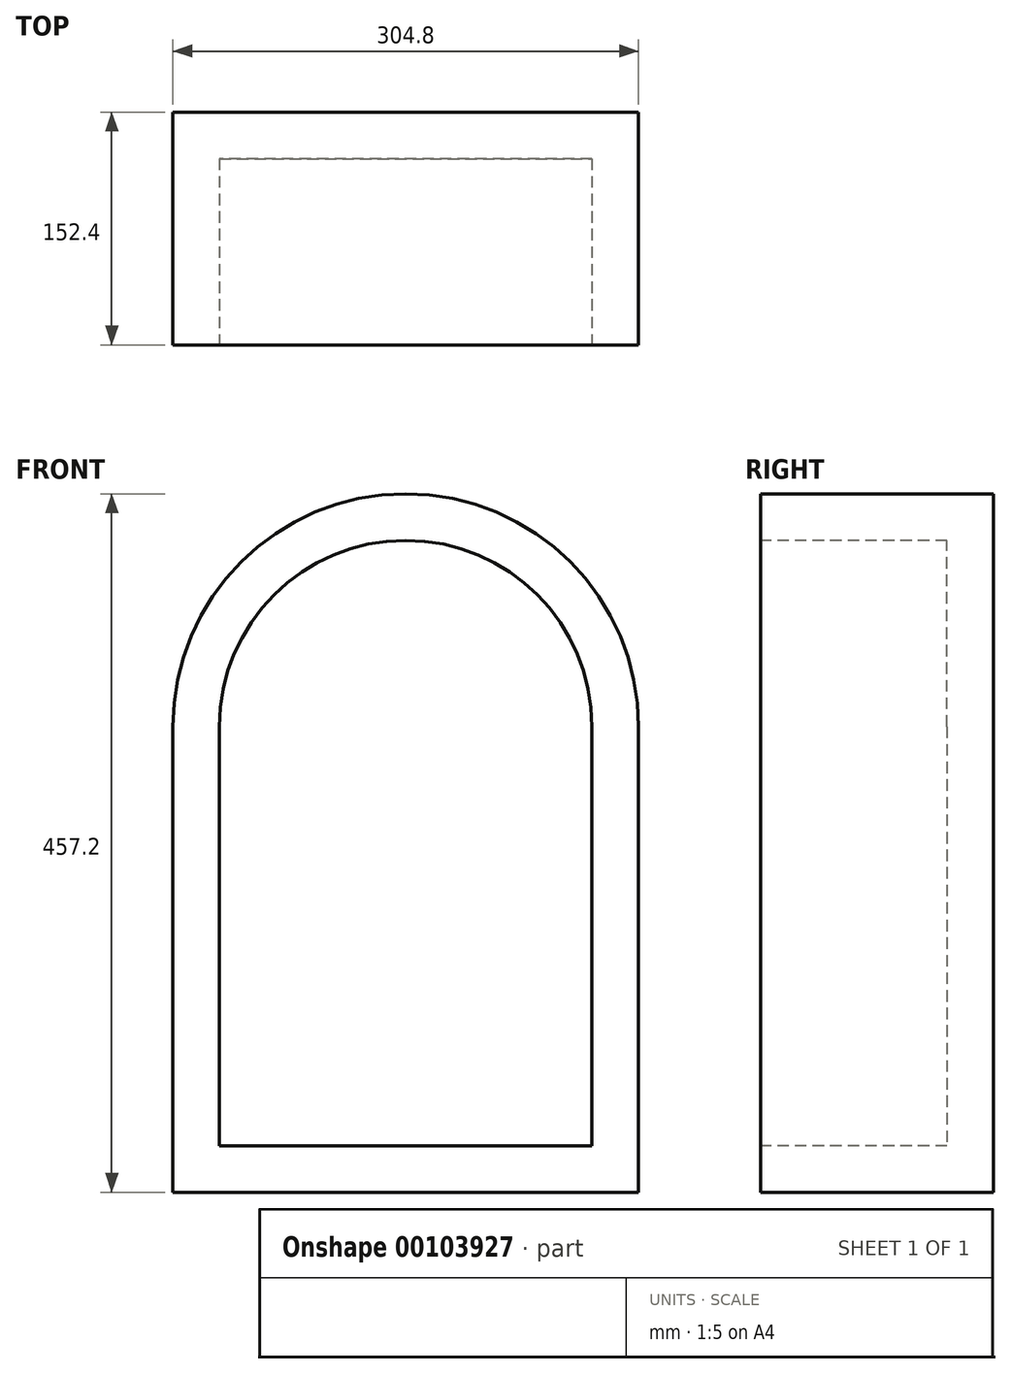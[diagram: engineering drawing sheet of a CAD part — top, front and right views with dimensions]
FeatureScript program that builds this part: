
annotation { "Feature Type Name" : "Feature", "Feature Type Description" : "" }
export const myFeature = defineFeature(function(context is Context, id is Id, definition is map)
    precondition{}
    {
        {
            var Q0;
            Q0=qCreatedBy(makeId("Front.planeOp"),FACE);
            var sketch = newSketch(context, id + "F0", { "sketchPlane" : qUnion([Q0])});
            skLineSegment(sketch, "E0.bottom", {"start": v(152.4, 152.4) * mm, "end": v(-152.4, 152.4) * mm});
            skLineSegment(sketch, "E0.top", {"start": v(152.4, -152.4) * mm, "end": v(-152.4, -152.4) * mm});
            skLineSegment(sketch, "E0.left", {"start": v(152.4, 152.4) * mm, "end": v(152.4, -152.4) * mm});
            skLineSegment(sketch, "E0.right", {"start": v(-152.4, 152.4) * mm, "end": v(-152.4, -152.4) * mm});
            skPoint(sketch, "E0.middle", {"position": v(0, 0) * mm});
            skSolve(sketch);
        }
        {
            var Q0;
            Q0 = qSketchRegion(id + "F0", true);
            extrude(context, id + "F1", {"entities" : qUnion([Q0]), "depth" : 152.4 * mm});
        }
        {
            var Q0;
            Q0=makeQuery(id+"F1.opExtrude","CAP_FACE",FACE,{"disambiguationData":[OSD([sQuery(id+"F0.wireOp",EDGE,"E0.bottom"),sQuery(id+"F0.wireOp",EDGE,"E0.top"),sQuery(id+"F0.wireOp",EDGE,"E0.left"),sQuery(id+"F0.wireOp",EDGE,"E0.right")])],"isStart":false});
            var sketch = newSketch(context, id + "F2", { "sketchPlane" : qUnion([Q0])});
            skArc(sketch, "E1", {"start": v(152.4, 152.4) * mm, "mid": v(0, 304.8) * mm, "end": v(-152.4, 152.4) * mm});
            skSolve(sketch);
        }
        {
            var Q0;
            Q0 = qSketchRegion(id + "F2", true);
            var Q1;
            Q1=makeQuery(id+"F2.imprint","IMPRINT",FACE,{"disambiguationData":[TD([[makeQuery(id+"F2.imprint","IMPRINT",EDGE,{"derivedFrom":sQuery(id+"F2.wireOp",EDGE,"E1")}),1.0]])]});
            extrude(context, id + "F3", {"entities" : qUnion([Q0, Q1]), "operationType" : NewBodyOperationType.ADD, "oppositeDirection" : true, "depth" : 152.4 * mm});
        }
        {
            var Q0;
            {var subQ0=sQuery(id+"F0.wireOp",EDGE,"E0.bottom");Q0=makeQuery(id+"F3.boolean.opBoolean","MERGE",FACE,{"derivedFrom":[makeQuery(id+"F1.opExtrude","CAP_FACE",FACE,{"disambiguationData":[OSD([subQ0,sQuery(id+"F0.wireOp",EDGE,"E0.top"),sQuery(id+"F0.wireOp",EDGE,"E0.left"),sQuery(id+"F0.wireOp",EDGE,"E0.right")])],"isStart":false}),makeQuery(id+"F3.opExtrude","CAP_FACE",FACE,{"disambiguationData":[OSD([subQ0,sQuery(id+"F2.wireOp",EDGE,"E1")])],"isStart":true})]});}
            var sketch = newSketch(context, id + "F4", { "sketchPlane" : qUnion([Q0])});
            skLineSegment(sketch, "E2", {"start": v(-121.92, -121.92) * mm, "end": v(121.92, -121.92) * mm});
            skLineSegment(sketch, "E3", {"start": v(121.92, -121.92) * mm, "end": v(121.92, 152.4) * mm});
            skLineSegment(sketch, "E4", {"start": v(-121.92, 152.4) * mm, "end": v(-121.92, -121.92) * mm});
            skArc(sketch, "E5", {"start": v(121.92, 152.4) * mm, "mid": v(0, 274.32) * mm, "end": v(-121.92, 152.4) * mm});
            skSolve(sketch);
        }
        {
            var Q0;
            Q0 = qSketchRegion(id + "F4", true);
            extrude(context, id + "F5", {"entities" : qUnion([Q0]), "operationType" : NewBodyOperationType.REMOVE, "oppositeDirection" : true, "depth" : 121.92 * mm});
        }
    });
